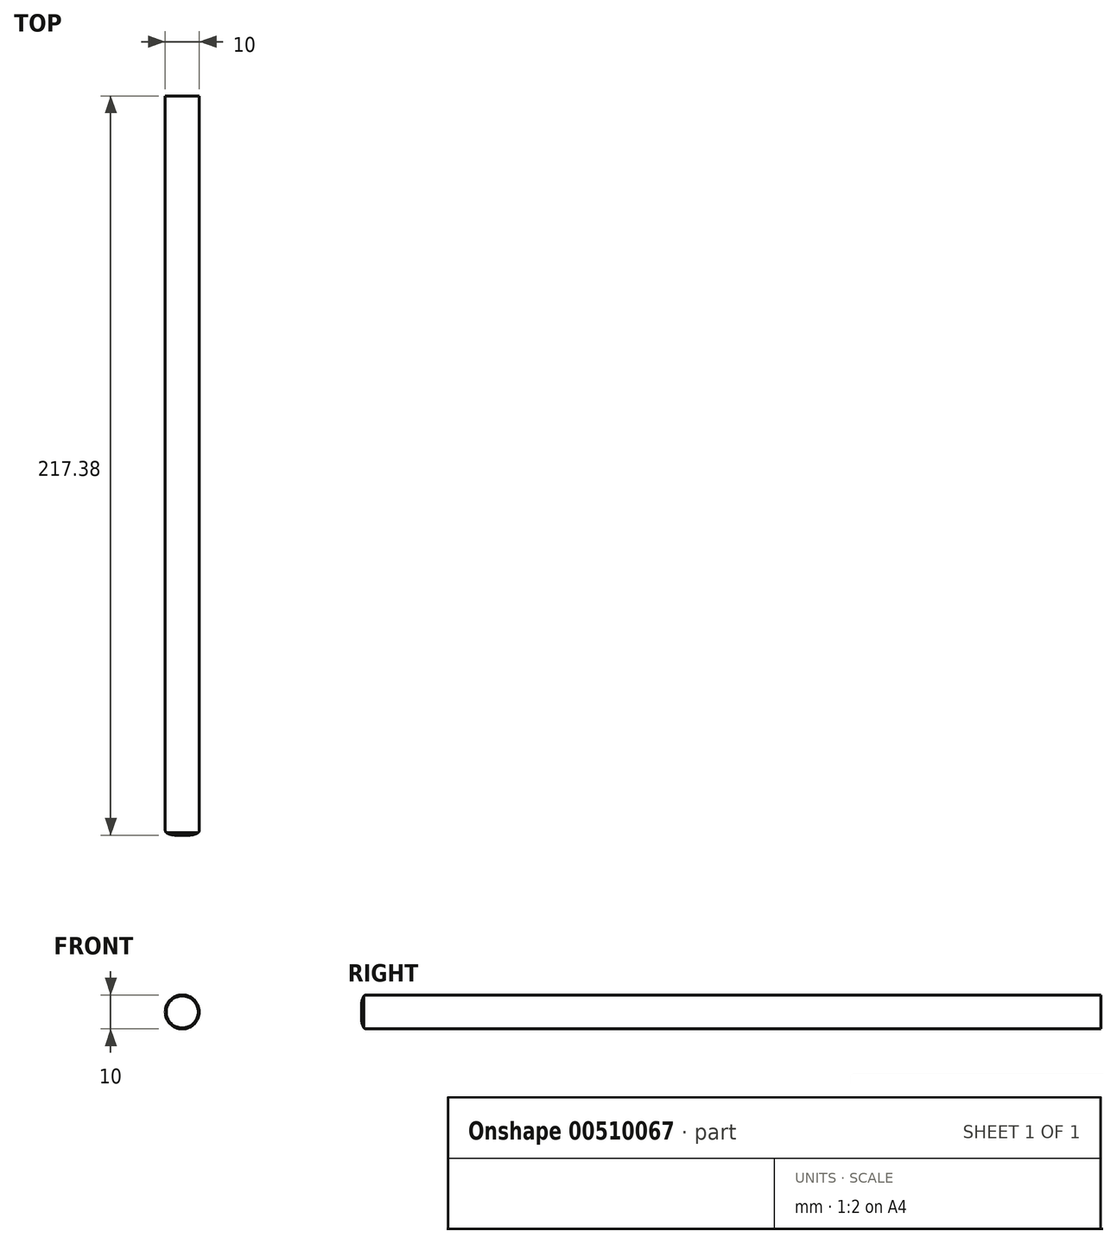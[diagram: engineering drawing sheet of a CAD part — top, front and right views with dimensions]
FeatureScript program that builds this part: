
annotation { "Feature Type Name" : "Feature", "Feature Type Description" : "" }
export const myFeature = defineFeature(function(context is Context, id is Id, definition is map)
    precondition{}
    {
        {
            var Q0;
            Q0=qCreatedBy(makeId("Front.planeOp"),FACE);
            var sketch = newSketch(context, id + "F0", { "sketchPlane" : qUnion([Q0])});
            skCircle(sketch, "E0", {"center": v(0, 0) * mm, "radius": 5 * mm});
            skSolve(sketch);
        }
        {
            var Q0;
            Q0=makeQuery(id+"F0.imprint","IMPRINT",FACE,{"disambiguationData":[TD([[makeQuery(id+"F0.imprint","IMPRINT",EDGE,{"derivedFrom":sQuery(id+"F0.wireOp",EDGE,"E0")}),1.0]])]});
            extrude(context, id + "F1", {"entities" : qUnion([Q0]), "depth" : 217.38 * mm});
        }
        {
            var Q0;
            Q0=makeQuery(id+"F1.opExtrude","CAP_EDGE",EDGE,{"disambiguationData":[OSD([sQuery(id+"F0.wireOp",EDGE,"E0")])],"isStart":false});
            chamfer(context, id + "F2", {"entities" : qUnion([Q0]), "width" : 1 * mm, "tangentPropagation" : true});
        }
        {
            var Q0;
            {var subQ0=sQuery(id+"F0.wireOp",EDGE,"E0");Q0=makeQuery(id+"F2.opChamfer","BLEND_EDGE",EDGE,{"blendedFrom":[makeQuery(id+"F1.opExtrude","CAP_EDGE",EDGE,{"disambiguationData":[OSD([subQ0])],"isStart":false}),makeQuery(id+"F1.opExtrude","SWEPT_FACE",FACE,{"disambiguationData":[OSD([subQ0])]})],"blendedInto":[makeQuery(id+"F1.opExtrude","SWEPT_FACE",FACE,{"disambiguationData":[OSD([subQ0])]})]});}
            fillet(context, id + "F3", {"entities" : qUnion([Q0]), "radius" : 1 * mm, "tangentPropagation" : true, "allowEdgeOverflow" : false});
        }
        {
            var Q0;
            {var subQ0=sQuery(id+"F0.wireOp",EDGE,"E0");Q0=makeQuery(id+"F2.opChamfer","BLEND_EDGE",EDGE,{"blendedFrom":[makeQuery(id+"F1.opExtrude","CAP_EDGE",EDGE,{"disambiguationData":[OSD([subQ0])],"isStart":false}),makeQuery(id+"F1.opExtrude","CAP_FACE",FACE,{"disambiguationData":[OSD([subQ0])],"isStart":false})],"blendedInto":[makeQuery(id+"F1.opExtrude","CAP_FACE",FACE,{"disambiguationData":[OSD([subQ0])],"isStart":false})]});}
            fillet(context, id + "F4", {"entities" : qUnion([Q0]), "radius" : 5 * mm, "tangentPropagation" : true, "allowEdgeOverflow" : false});
        }
    });
